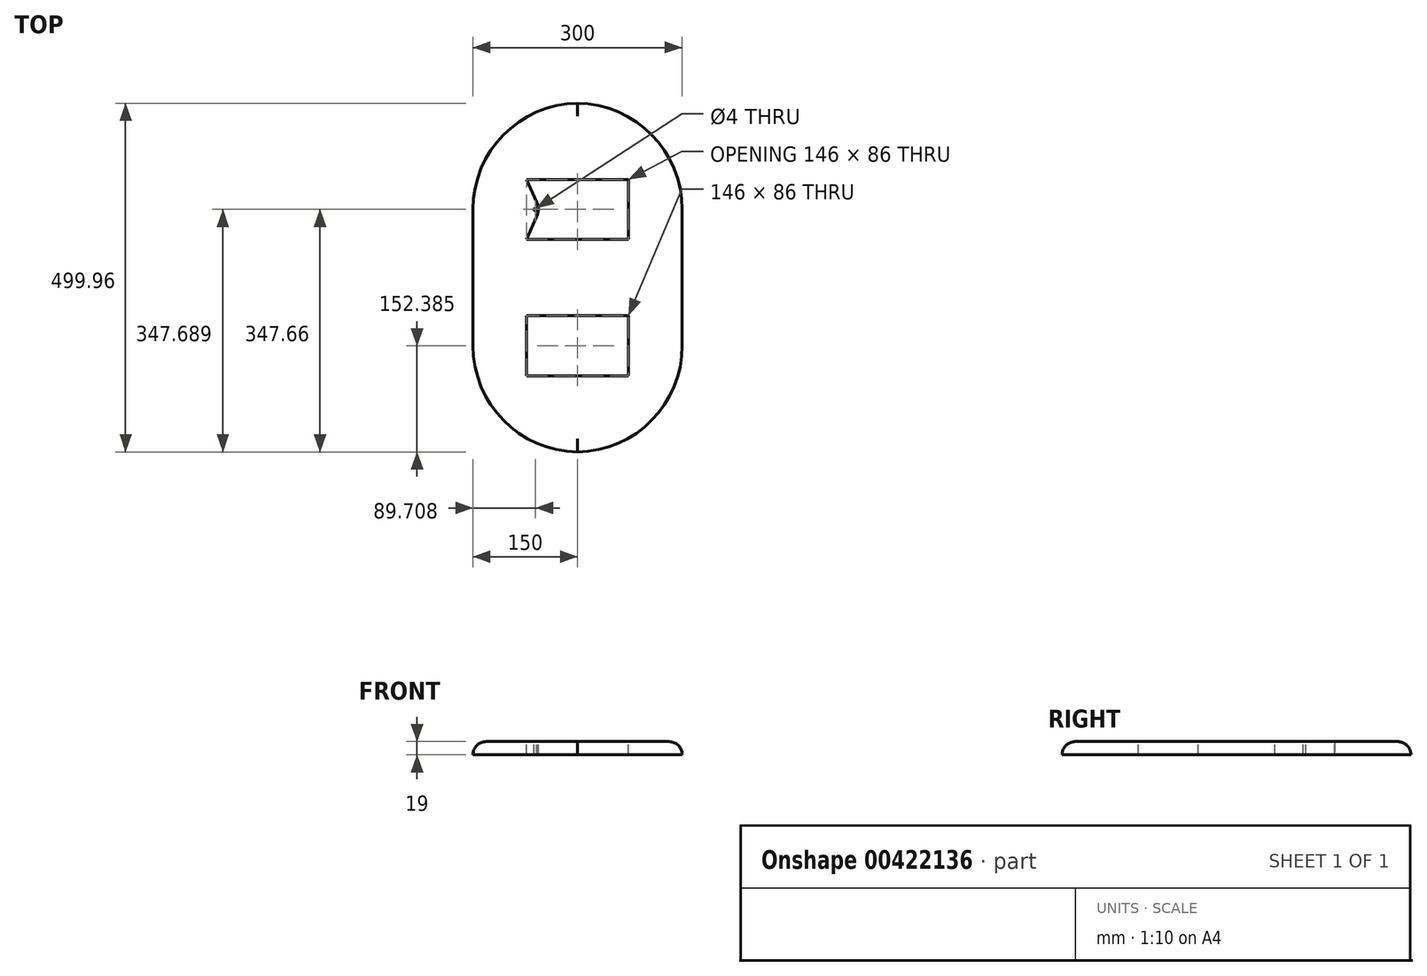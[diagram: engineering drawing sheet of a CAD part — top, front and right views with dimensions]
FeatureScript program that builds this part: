
annotation { "Feature Type Name" : "Feature", "Feature Type Description" : "" }
export const myFeature = defineFeature(function(context is Context, id is Id, definition is map)
    precondition{}
    {
        {
            var Q0;
            Q0=qCreatedBy(makeId("Top.planeOp"),FACE);
            var sketch = newSketch(context, id + "F0", { "sketchPlane" : qUnion([Q0])});
            skLineSegment(sketch, "E0.bottom", {"start": v(150, 250) * mm, "end": v(-150, 250) * mm});
            skLineSegment(sketch, "E0.top", {"start": v(150, -250) * mm, "end": v(-150, -250) * mm});
            skLineSegment(sketch, "E0.left", {"start": v(150, 250) * mm, "end": v(150, -250) * mm});
            skLineSegment(sketch, "E0.right", {"start": v(-150, 250) * mm, "end": v(-150, -250) * mm});
            skPoint(sketch, "E0.middle", {"position": v(0, 0) * mm});
            skSolve(sketch);
        }
        {
            var Q0;
            Q0=makeQuery(id+"F0.imprint","IMPRINT",FACE,{"disambiguationData":[TD([[makeQuery(id+"F0.imprint","IMPRINT",EDGE,{"derivedFrom":sQuery(id+"F0.wireOp",EDGE,"E0.bottom")}),1.0]])]});
            extrude(context, id + "F1", {"entities" : qUnion([Q0]), "depth" : 19 * mm});
        }
        {
            var Q0;
            Q0=makeQuery(id+"F1.opExtrude","SWEPT_EDGE",EDGE,{"disambiguationData":[OSD([sQuery(id+"F0.wireOp",EDGE,"E0.top"),sQuery(id+"F0.wireOp",EDGE,"E0.right")])]});
            var Q1;
            Q1=makeQuery(id+"F1.opExtrude","SWEPT_EDGE",EDGE,{"disambiguationData":[OSD([sQuery(id+"F0.wireOp",EDGE,"E0.top"),sQuery(id+"F0.wireOp",EDGE,"E0.left")])]});
            var Q2;
            Q2=makeQuery(id+"F1.opExtrude","SWEPT_EDGE",EDGE,{"disambiguationData":[OSD([sQuery(id+"F0.wireOp",EDGE,"E0.bottom"),sQuery(id+"F0.wireOp",EDGE,"E0.right")])]});
            var Q3;
            Q3=makeQuery(id+"F1.opExtrude","SWEPT_EDGE",EDGE,{"disambiguationData":[OSD([sQuery(id+"F0.wireOp",EDGE,"E0.bottom"),sQuery(id+"F0.wireOp",EDGE,"E0.left")])]});
            fillet(context, id + "F2", {"entities" : qUnion([Q0, Q1, Q2, Q3]), "radius" : 152.4 * mm, "tangentPropagation" : true, "allowEdgeOverflow" : false});
        }
        {
            var Q0;
            Q0=makeQuery(id+"F1.opExtrude","CAP_EDGE",EDGE,{"disambiguationData":[OSD([sQuery(id+"F0.wireOp",EDGE,"E0.left")])],"isStart":false});
            var Q1;
            {var subQ0=sQuery(id+"F0.wireOp",EDGE,"E0.left");var subQ1=sQuery(id+"F0.wireOp",EDGE,"E0.bottom");Q1=makeQuery(id+"F2.opFillet","BLEND_EDGE",EDGE,{"blendedFrom":[makeQuery(id+"F1.opExtrude","SWEPT_EDGE",EDGE,{"disambiguationData":[OSD([subQ1,subQ0])]}),makeQuery(id+"F1.opExtrude","CAP_FACE",FACE,{"disambiguationData":[OSD([subQ1,sQuery(id+"F0.wireOp",EDGE,"E0.top"),subQ0,sQuery(id+"F0.wireOp",EDGE,"E0.right")])],"isStart":false})],"blendedInto":[makeQuery(id+"F1.opExtrude","CAP_FACE",FACE,{"disambiguationData":[OSD([subQ1,sQuery(id+"F0.wireOp",EDGE,"E0.top"),subQ0,sQuery(id+"F0.wireOp",EDGE,"E0.right")])],"isStart":false})]});}
            var Q2;
            {var subQ0=sQuery(id+"F0.wireOp",EDGE,"E0.right");var subQ1=sQuery(id+"F0.wireOp",EDGE,"E0.bottom");Q2=makeQuery(id+"F2.opFillet","BLEND_EDGE",EDGE,{"blendedFrom":[makeQuery(id+"F1.opExtrude","SWEPT_EDGE",EDGE,{"disambiguationData":[OSD([subQ1,subQ0])]}),makeQuery(id+"F1.opExtrude","CAP_FACE",FACE,{"disambiguationData":[OSD([subQ1,sQuery(id+"F0.wireOp",EDGE,"E0.top"),sQuery(id+"F0.wireOp",EDGE,"E0.left"),subQ0])],"isStart":false})],"blendedInto":[makeQuery(id+"F1.opExtrude","CAP_FACE",FACE,{"disambiguationData":[OSD([subQ1,sQuery(id+"F0.wireOp",EDGE,"E0.top"),sQuery(id+"F0.wireOp",EDGE,"E0.left"),subQ0])],"isStart":false})]});}
            var Q3;
            Q3=makeQuery(id+"F1.opExtrude","CAP_EDGE",EDGE,{"disambiguationData":[OSD([sQuery(id+"F0.wireOp",EDGE,"E0.right")])],"isStart":false});
            var Q4;
            {var subQ0=sQuery(id+"F0.wireOp",EDGE,"E0.right");var subQ1=sQuery(id+"F0.wireOp",EDGE,"E0.top");Q4=makeQuery(id+"F2.opFillet","BLEND_EDGE",EDGE,{"blendedFrom":[makeQuery(id+"F1.opExtrude","SWEPT_EDGE",EDGE,{"disambiguationData":[OSD([subQ1,subQ0])]}),makeQuery(id+"F1.opExtrude","CAP_FACE",FACE,{"disambiguationData":[OSD([sQuery(id+"F0.wireOp",EDGE,"E0.bottom"),subQ1,sQuery(id+"F0.wireOp",EDGE,"E0.left"),subQ0])],"isStart":false})],"blendedInto":[makeQuery(id+"F1.opExtrude","CAP_FACE",FACE,{"disambiguationData":[OSD([sQuery(id+"F0.wireOp",EDGE,"E0.bottom"),subQ1,sQuery(id+"F0.wireOp",EDGE,"E0.left"),subQ0])],"isStart":false})]});}
            var Q5;
            {var subQ0=sQuery(id+"F0.wireOp",EDGE,"E0.left");var subQ1=sQuery(id+"F0.wireOp",EDGE,"E0.top");Q5=makeQuery(id+"F2.opFillet","BLEND_EDGE",EDGE,{"blendedFrom":[makeQuery(id+"F1.opExtrude","SWEPT_EDGE",EDGE,{"disambiguationData":[OSD([subQ1,subQ0])]}),makeQuery(id+"F1.opExtrude","CAP_FACE",FACE,{"disambiguationData":[OSD([sQuery(id+"F0.wireOp",EDGE,"E0.bottom"),subQ1,subQ0,sQuery(id+"F0.wireOp",EDGE,"E0.right")])],"isStart":false})],"blendedInto":[makeQuery(id+"F1.opExtrude","CAP_FACE",FACE,{"disambiguationData":[OSD([sQuery(id+"F0.wireOp",EDGE,"E0.bottom"),subQ1,subQ0,sQuery(id+"F0.wireOp",EDGE,"E0.right")])],"isStart":false})]});}
            fillet(context, id + "F3", {"entities" : qUnion([Q0, Q1, Q2, Q3, Q4, Q5]), "radius" : 19 * mm, "tangentPropagation" : true, "allowEdgeOverflow" : false});
        }
        {
            var Q0;
            Q0=makeQuery(id+"F1.opExtrude","CAP_FACE",FACE,{"disambiguationData":[OSD([sQuery(id+"F0.wireOp",EDGE,"E0.bottom"),sQuery(id+"F0.wireOp",EDGE,"E0.top"),sQuery(id+"F0.wireOp",EDGE,"E0.left"),sQuery(id+"F0.wireOp",EDGE,"E0.right")])],"isStart":false});
            var sketch = newSketch(context, id + "F4", { "sketchPlane" : qUnion([Q0])});
            skLineSegment(sketch, "E1", {"start": v(131, 97.6) * mm, "end": v(-131, 97.6) * mm});
            skLineSegment(sketch, "E2", {"start": v(-131, 97.6) * mm, "end": v(0, 230.98) * mm});
            skLineSegment(sketch, "E3", {"start": v(0, 230.98) * mm, "end": v(0, -236.1) * mm});
            skLineSegment(sketch, "E4", {"start": v(0, -236.1) * mm, "end": v(131, -97.6) * mm});
            skLineSegment(sketch, "E5", {"start": v(131, -97.6) * mm, "end": v(-131, -97.6) * mm});
            skSolve(sketch);
        }
        {
            var Q0;
            {var subQ0=sQuery(id+"F4.wireOp",EDGE,"E1");var subQ7=sQuery(id+"F4.wireOp",EDGE,"E3");var subQ8=makeQuery(id+"F4.imprint","INTERSECT",VERTEX,{"derivedFrom":[subQ0,subQ7]});Q0=makeQuery(id+"F4.imprint","IMPRINT",FACE,{"disambiguationData":[TD([[makeQuery(id+"F4.imprint","IMPRINT",EDGE,{"disambiguationData":[TD([[subQ8,-1.0]])],"derivedFrom":subQ7}),1.0]])]});}
            var sketch = newSketch(context, id + "F5", { "sketchPlane" : qUnion([Q0])});
            skLineSegment(sketch, "E6.bottom", {"start": v(73, 54.68) * mm, "end": v(-73, 54.68) * mm});
            skLineSegment(sketch, "E6.top", {"start": v(73, 140.68) * mm, "end": v(-73, 140.68) * mm});
            skLineSegment(sketch, "E6.left", {"start": v(73, 54.68) * mm, "end": v(73, 140.68) * mm});
            skLineSegment(sketch, "E6.right", {"start": v(-73, 54.68) * mm, "end": v(-73, 140.68) * mm});
            skPoint(sketch, "E6.middle", {"position": v(0, 97.68) * mm});
            skSolve(sketch);
        }
        {
            var Q0;
            {var subQ0=sQuery(id+"F4.wireOp",EDGE,"E1");var subQ7=sQuery(id+"F4.wireOp",EDGE,"E3");var subQ8=makeQuery(id+"F4.imprint","INTERSECT",VERTEX,{"derivedFrom":[subQ0,subQ7]});Q0=makeQuery(id+"F4.imprint","IMPRINT",FACE,{"disambiguationData":[TD([[makeQuery(id+"F4.imprint","IMPRINT",EDGE,{"disambiguationData":[TD([[subQ8,-1.0]])],"derivedFrom":subQ7}),1.0]])]});}
            var sketch = newSketch(context, id + "F6", { "sketchPlane" : qUnion([Q0])});
            skLineSegment(sketch, "E7.bottom", {"start": v(73, -140.6) * mm, "end": v(-73, -140.6) * mm});
            skLineSegment(sketch, "E7.top", {"start": v(73, -54.6) * mm, "end": v(-73, -54.6) * mm});
            skLineSegment(sketch, "E7.left", {"start": v(73, -140.6) * mm, "end": v(73, -54.6) * mm});
            skLineSegment(sketch, "E7.right", {"start": v(-73, -140.6) * mm, "end": v(-73, -54.6) * mm});
            skPoint(sketch, "E7.middle", {"position": v(0, -97.6) * mm});
            skSolve(sketch);
        }
        {
            var Q0;
            Q0 = qSketchRegion(id + "F6", true);
            var Q1;
            Q1 = qSketchRegion(id + "F5", true);
            extrude(context, id + "F7", {"entities" : qUnion([Q0, Q1]), "operationType" : NewBodyOperationType.REMOVE, "oppositeDirection" : true, "depth" : 20 * mm});
        }
        {
            var Q0;
            {var subQ0=sQuery(id+"F4.wireOp",EDGE,"E1");var subQ7=sQuery(id+"F4.wireOp",EDGE,"E3");var subQ8=makeQuery(id+"F4.imprint","INTERSECT",VERTEX,{"derivedFrom":[subQ0,subQ7]});Q0=makeQuery(id+"F4.imprint","IMPRINT",FACE,{"disambiguationData":[TD([[makeQuery(id+"F4.imprint","IMPRINT",EDGE,{"disambiguationData":[TD([[subQ8,-1.0]])],"derivedFrom":subQ7}),-1.0]])]});}
            var sketch = newSketch(context, id + "F8", { "sketchPlane" : qUnion([Q0])});
            skCircle(sketch, "E8", {"center": v(-60.3, 97.7) * mm, "radius": 2 * mm});
            skCircle(sketch, "E9", {"center": v(60.3, 97.7) * mm, "radius": 2 * mm});
            skSolve(sketch);
        }
        {
            var Q0;
            {var subQ0=sQuery(id+"F4.wireOp",EDGE,"E1");var subQ7=sQuery(id+"F4.wireOp",EDGE,"E3");var subQ8=makeQuery(id+"F4.imprint","INTERSECT",VERTEX,{"derivedFrom":[subQ0,subQ7]});Q0=makeQuery(id+"F4.imprint","IMPRINT",FACE,{"disambiguationData":[TD([[makeQuery(id+"F4.imprint","IMPRINT",EDGE,{"disambiguationData":[TD([[subQ8,-1.0]])],"derivedFrom":subQ7}),-1.0]])]});}
            var sketch = newSketch(context, id + "F9", { "sketchPlane" : qUnion([Q0])});
            skLineSegment(sketch, "E10", {"start": v(-73, 140.68) * mm, "end": v(-53.86, 97.81) * mm});
            skLineSegment(sketch, "E11", {"start": v(-53.86, 97.81) * mm, "end": v(-73.27, 54.1) * mm});
            skLineSegment(sketch, "E12", {"start": v(-73.27, 54.1) * mm, "end": v(-73, 140.68) * mm});
            skSolve(sketch);
        }
        {
            var Q0;
            Q0 = qSketchRegion(id + "F9", true);
            extrude(context, id + "F10", {"entities" : qUnion([Q0]), "operationType" : NewBodyOperationType.ADD, "depth" : -19 * mm});
        }
        {
            var Q0;
            Q0 = qSketchRegion(id + "F8", true);
            extrude(context, id + "F11", {"entities" : qUnion([Q0]), "operationType" : NewBodyOperationType.REMOVE, "oppositeDirection" : true, "depth" : 19 * mm});
        }
        {
            var Q0;
            Q0=makeQuery(id+"F10.opExtrude","SWEPT_EDGE",EDGE,{"disambiguationData":[OSD([sQuery(id+"F9.wireOp",EDGE,"E10"),sQuery(id+"F9.wireOp",EDGE,"E11")])]});
            fillet(context, id + "F12", {"entities" : qUnion([Q0]), "radius" : 25 * mm, "tangentPropagation" : true, "allowEdgeOverflow" : false});
        }
    });
